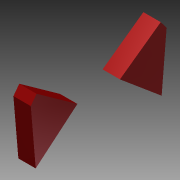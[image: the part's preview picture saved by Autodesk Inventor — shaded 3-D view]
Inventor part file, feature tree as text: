
AUTODESK INVENTOR PART (.ipt)
format: ipt  version: 2014 (Build 180170000, 170)  size: 769,024 bytes
history: native  units: in
note: dims shown in document units (in); Inventor stores cm internally (conversion verified against a paired STEP export)
features: sketch x22, extrude x15, plane x9, projected_geometry x6, loft x4, other x3, mirror x1, emboss x1
ambient origin geometry x8: Origin, YZ Plane, XZ Plane, XY Plane, X Axis, Y Axis, Z Axis, Center Point
bodies: Solid1 (feature_tree)
feature tree (61):
  sketch  "Sketch1"  dims[d0=0.7559in d1=0.7559in]
  plane  "Work Plane1"
  loft  "Loft1"
  extrude  "Extrusion1"  Depth=0.2in
  plane  "Work Plane4"
  loft  "Loft2"
  plane  "Work Plane5"
  loft  "Loft3"
  loft  "Loft4"
  extrude  "Extrusion2"  TaperAngle=0.0deg  [1 undecoded]
  plane  "Work Plane6"
  extrude  "Extrusion3"  Depth=1.0in
  extrude  "Extrusion4"  Depth=1.0651in
  extrude  "Extrusion5"  Depth=0.962in
  plane  "Work Plane7"
  extrude  "Extrusion6"  Depth=0.075in
  plane  "Work Plane8"
  other  "Work Axis1"
  plane  "Work Plane9"
  extrude  "Extrusion7"  Depth=0.06in
  mirror  "Mirror3"
  extrude  "Extrusion8"  Depth=0.1in
  plane  "Work Plane10"
  extrude  "Extrusion9"  Depth=0.0625in
  plane  "Work Plane11"
  extrude  "Extrusion10"  Depth=0.075in
  extrude  "Extrusion11"  TaperAngle=0.0deg  [1 undecoded]
  extrude  "Extrusion12"  Depth=0.2in
  extrude  "Extrusion13"  TaperAngle=0.0deg  [1 undecoded]
  emboss  "Emboss1"
  extrude  "Extrusion15"  Depth=0.01in
  extrude  "Extrusion16"  Depth=0.0344in
  sketch  "Sketch2"  dims[d2=0.9963in d3=0.2in]
  sketch  "Sketch3"  dims[d4=0.5in d6=0.08in]
  sketch  "Sketch4"  dims[d7=0.55in d8=150.0deg]
  other  "Edges1"
  sketch  "Sketch5"  dims[d9=150.0deg d14=0.33in]
  projected_geometry  "Projected Loop1"
  other  "Edges2"
  sketch  "Sketch6"  dims[d15=0.66in d18=0.0in d19=90.0deg]
  sketch  "Sketch7"  dims[d20=0.0in d21=90.0deg d22=1.0in]
  sketch  "Sketch8"  dims[d26=1.0651in d28=1.0651in]
  sketch  "Sketch9"  dims[d29=0.0in d30=0.962in]
  sketch  "Sketch10"  dims[d31=0.962in d32=0.075in]
  sketch  "Sketch11"  dims[d33=0.15in d34=0.06in]
  sketch  "Sketch12"  dims[d35=0.1in d36=0.05in]
  sketch  "Sketch13"  dims[d37=0.45in d38=0.0in d39=0.0625in]
  projected_geometry  "Projected Loop2"
  projected_geometry  "Projected Loop3"
  sketch  "Sketch14"  dims[d40=0.01in d41=0.075in]
  projected_geometry  "Projected Loop4"
  sketch  "Sketch15"  dims[d42=0.01in d43=0.0in d44=90.0deg]
  sketch  "Sketch16"  dims[d45=0.0in d46=90.0deg d47=0.2in]
  sketch  "Sketch17"  dims[d48=0.07in d49=0.0in d50=90.0deg]
  sketch  "Sketch18"  dims[d51=0.0in d52=90.0deg d53=0.01in]
  sketch  "Sketch19"  dims[d54=0.01in d55=0.0344in]
  sketch  "Sketch20"  dims[d56=150.0deg]
  sketch  "Sketch22"  dims[d57=60.0deg]
  projected_geometry  "Projected Loop5"
  sketch  "Sketch23"  dims[d58=150.0deg d59=0.7in d60=0.05in d61=0.05in d62=0.05in d63=0.05in d64=0.05in d65=0.01in d66=0.0in d67=90.0deg d68=0.0in d69=90.0deg d70=0.1in d71=0.4in d72=0.15in d73=0.05in d74=0.0in d75=0.02in d77=0.15in d78=0.02in d79=0.1in d80=0.1in d81=0.1in d82=0.02in d83=0.15in d84=0.05in d85=0.0in d86=0.045in d87=0.0in d88=0.025in d89=0.0in d90=0.02in d91=0.02in d92=0.005in d93=0.0in d94=90.0deg d95=0.4466in d96=1.0in d97=0.0in d98=1.0in d99=0.0in d100=0.6528in d101=0.0in d102=0.0in d103=1.0in d104=0.0in d106=90.0deg d107=1.0in d108=0.0in d109=1.65in d110=0.1in d111=0.075in d112=0.0in d113=0.1in d114=0.075in d115=0.0in d116=0.05in d117=0.0in d121=0.05in d122=0.0in d123=0.1in d124=0.0in]
  projected_geometry  "Projected Loop6"
note: 3 required parameter values undecoded (feature->parameter linkage not recoverable at this tier; creation-order binding heuristic only, values carry confidence <= 0.55)
